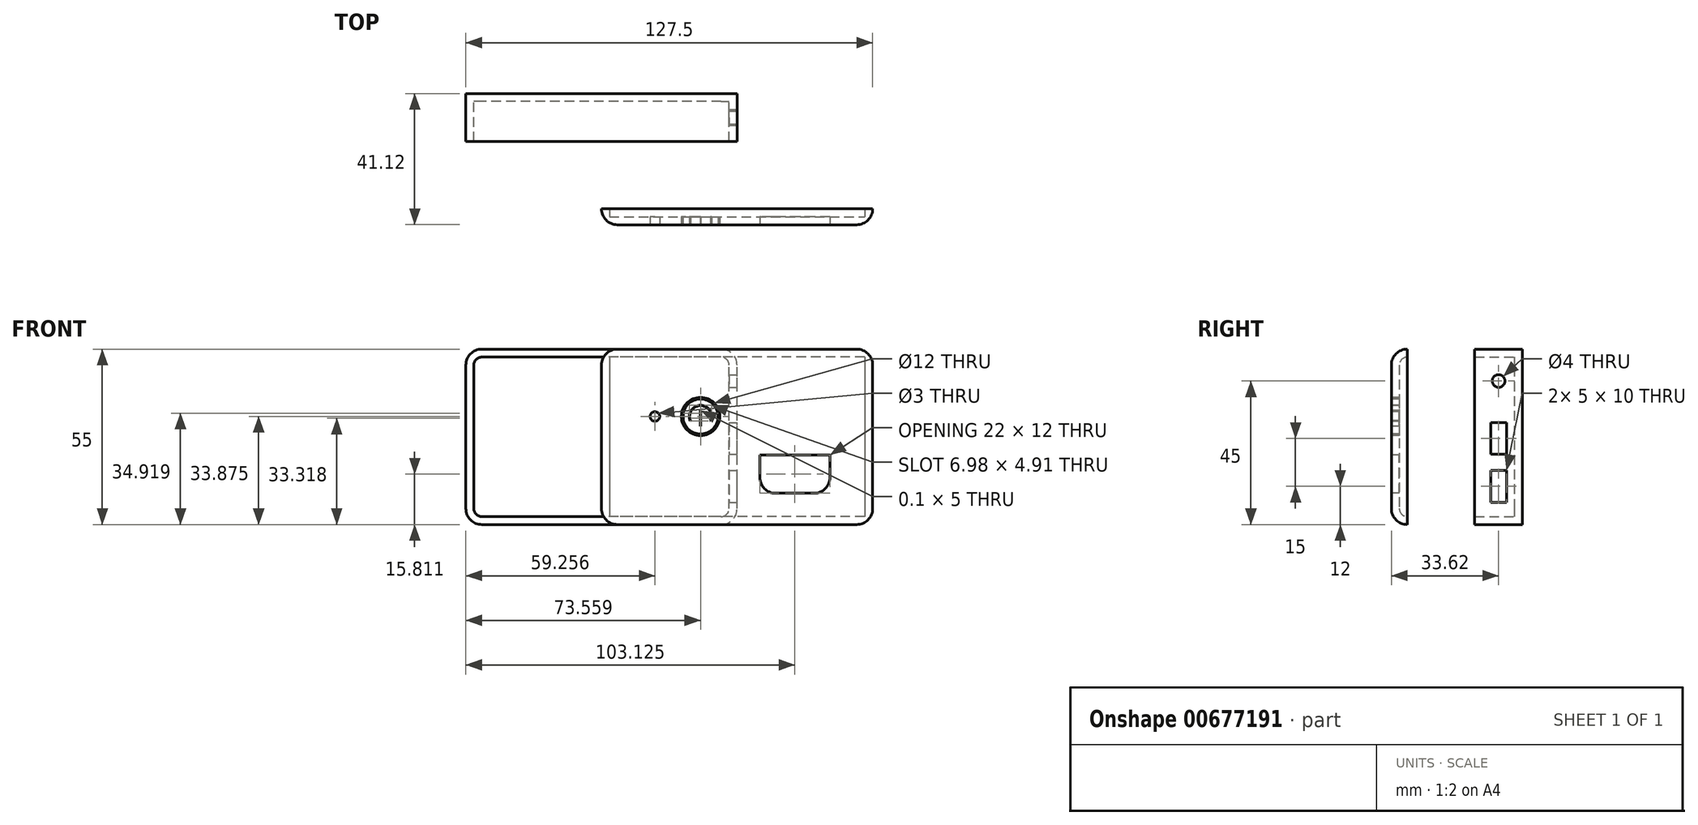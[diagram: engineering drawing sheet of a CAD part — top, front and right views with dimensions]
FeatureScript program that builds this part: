
annotation { "Feature Type Name" : "Feature", "Feature Type Description" : "" }
export const myFeature = defineFeature(function(context is Context, id is Id, definition is map)
    precondition{}
    {
        {
            var Q0;
            Q0=qCreatedBy(makeId("Front.planeOp"),FACE);
            var sketch = newSketch(context, id + "F0", { "sketchPlane" : qUnion([Q0])});
            skLineSegment(sketch, "E0.bottom", {"start": v(42.5, -27.5) * mm, "end": v(-42.5, -27.5) * mm});
            skLineSegment(sketch, "E0.top", {"start": v(42.5, 27.5) * mm, "end": v(-42.5, 27.5) * mm});
            skLineSegment(sketch, "E0.left", {"start": v(42.5, -27.5) * mm, "end": v(42.5, 27.5) * mm});
            skLineSegment(sketch, "E0.right", {"start": v(-42.5, -27.5) * mm, "end": v(-42.5, 27.5) * mm});
            skPoint(sketch, "E0.middle", {"position": v(0, 0) * mm});
            skSolve(sketch);
        }
        {
            var Q0;
            Q0 = qSketchRegion(id + "F0", true);
            extrude(context, id + "F1", {"entities" : qUnion([Q0]), "endBound" : BoundingType.SYMMETRIC, "depth" : 15 * mm, "offsetDistance" : 25 * mm});
        }
        {
            var Q0;
            Q0=makeQuery(id+"F1.opExtrude","SWEPT_EDGE",EDGE,{"disambiguationData":[OSD([sQuery(id+"F0.wireOp",EDGE,"E0.top"),sQuery(id+"F0.wireOp",EDGE,"E0.right")])]});
            var Q1;
            Q1=makeQuery(id+"F1.opExtrude","SWEPT_EDGE",EDGE,{"disambiguationData":[OSD([sQuery(id+"F0.wireOp",EDGE,"E0.top"),sQuery(id+"F0.wireOp",EDGE,"E0.left")])]});
            var Q2;
            Q2=makeQuery(id+"F1.opExtrude","SWEPT_EDGE",EDGE,{"disambiguationData":[OSD([sQuery(id+"F0.wireOp",EDGE,"E0.bottom"),sQuery(id+"F0.wireOp",EDGE,"E0.left")])]});
            var Q3;
            Q3=makeQuery(id+"F1.opExtrude","SWEPT_EDGE",EDGE,{"disambiguationData":[OSD([sQuery(id+"F0.wireOp",EDGE,"E0.bottom"),sQuery(id+"F0.wireOp",EDGE,"E0.right")])]});
            fillet(context, id + "F2", {"entities" : qUnion([Q0, Q1, Q2, Q3]), "radius" : 5 * mm, "tangentPropagation" : true, "allowEdgeOverflow" : false});
        }
        {
            var Q0;
            Q0=makeQuery(id+"F1.opExtrude","CAP_FACE",FACE,{"disambiguationData":[OSD([sQuery(id+"F0.wireOp",EDGE,"E0.bottom"),sQuery(id+"F0.wireOp",EDGE,"E0.top"),sQuery(id+"F0.wireOp",EDGE,"E0.left"),sQuery(id+"F0.wireOp",EDGE,"E0.right")])],"isStart":false});
            shell(context, id + "F3", {"entities" : qUnion([Q0]), "thickness" : 2.5 * mm});
        }
        {
            var Q0;
            Q0=makeQuery(id+"F1.opExtrude","SWEPT_FACE",FACE,{"disambiguationData":[OSD([sQuery(id+"F0.wireOp",EDGE,"E0.left")])]});
            var sketch = newSketch(context, id + "F4", { "sketchPlane" : qUnion([Q0])});
            skLineSegment(sketch, "E1.bottom", {"start": v(2.5, -20.5) * mm, "end": v(-2.5, -20.5) * mm});
            skLineSegment(sketch, "E1.top", {"start": v(2.5, -10.5) * mm, "end": v(-2.5, -10.5) * mm});
            skLineSegment(sketch, "E1.left", {"start": v(2.5, -20.5) * mm, "end": v(2.5, -10.5) * mm});
            skLineSegment(sketch, "E1.right", {"start": v(-2.5, -20.5) * mm, "end": v(-2.5, -10.5) * mm});
            skPoint(sketch, "E1.middle", {"position": v(0, -15.5) * mm});
            skLineSegment(sketch, "E2.bottom", {"start": v(2.5, -5.5) * mm, "end": v(-2.5, -5.5) * mm});
            skLineSegment(sketch, "E2.top", {"start": v(2.5, 4.5) * mm, "end": v(-2.5, 4.5) * mm});
            skLineSegment(sketch, "E2.left", {"start": v(2.5, -5.5) * mm, "end": v(2.5, 4.5) * mm});
            skLineSegment(sketch, "E2.right", {"start": v(-2.5, -5.5) * mm, "end": v(-2.5, 4.5) * mm});
            skPoint(sketch, "E2.middle", {"position": v(0, -0.5) * mm});
            skSolve(sketch);
        }
        {
            var Q0;
            Q0 = qSketchRegion(id + "F4", true);
            extrude(context, id + "F5", {"entities" : qUnion([Q0]), "operationType" : NewBodyOperationType.REMOVE, "oppositeDirection" : true, "depth" : 25 * mm, "offsetDistance" : 25 * mm});
        }
        {
            var Q0;
            Q0=makeQuery(id+"F1.opExtrude","SWEPT_FACE",FACE,{"disambiguationData":[OSD([sQuery(id+"F0.wireOp",EDGE,"E0.left")])]});
            var sketch = newSketch(context, id + "F6", { "sketchPlane" : qUnion([Q0])});
            skCircle(sketch, "E3", {"center": v(0, 17.5) * mm, "radius": 2 * mm});
            skSolve(sketch);
        }
        {
            var Q0;
            Q0 = qSketchRegion(id + "F6", true);
            extrude(context, id + "F7", {"entities" : qUnion([Q0]), "operationType" : NewBodyOperationType.REMOVE, "oppositeDirection" : true, "depth" : 25 * mm, "offsetDistance" : 25 * mm});
        }
        {
            var Q0;
            Q0=qCreatedBy(makeId("Right.planeOp"),FACE);
            var sketch = newSketch(context, id + "F8", { "sketchPlane" : qUnion([Q0])});
            skLineSegment(sketch, "E4", {"start": v(-28.62, 27.5) * mm, "end": v(-28.62, -27.5) * mm});
            skLineSegment(sketch, "E5", {"start": v(-33.62, 22.5) * mm, "end": v(-33.62, -22.5) * mm});
            skArc(sketch, "E6", {"start": v(-28.62, 27.5) * mm, "mid": v(-32.16, 26.04) * mm, "end": v(-33.62, 22.5) * mm});
            skArc(sketch, "E7", {"start": v(-33.62, -22.5) * mm, "mid": v(-32.16, -26.04) * mm, "end": v(-28.62, -27.5) * mm});
            skSolve(sketch);
        }
        {
            var Q0;
            Q0 = qSketchRegion(id + "F8", true);
            extrude(context, id + "F9", {"entities" : qUnion([Q0]), "depth" : 85 * mm, "offsetDistance" : 25 * mm});
        }
        {
            var Q0;
            Q0=makeQuery(id+"F9.opExtrude","SWEPT_FACE",FACE,{"disambiguationData":[OSD([sQuery(id+"F8.wireOp",EDGE,"E4")])]});
            shell(context, id + "F10", {"entities" : qUnion([Q0]), "thickness" : 2.5 * mm});
        }
        {
            var Q0;
            Q0=makeQuery(id+"F9.opExtrude","SWEPT_FACE",FACE,{"disambiguationData":[OSD([sQuery(id+"F8.wireOp",EDGE,"E5")])]});
            var sketch = newSketch(context, id + "F11", { "sketchPlane" : qUnion([Q0])});
            skCircle(sketch, "E8", {"center": v(31.06, 6.37) * mm, "radius": 6 * mm});
            skCircle(sketch, "E9", {"center": v(16.76, 6.37) * mm, "radius": 1.5 * mm});
            skCircle(sketch, "E10", {"center": v(31.06, 6.37) * mm, "radius": 5.5 * mm});
            skArc(sketch, "E11", {"start": v(34.02, 4.1) * mm, "mid": v(31.19, 10.06) * mm, "end": v(27.93, 4.32) * mm});
            skLineSegment(sketch, "E12", {"start": v(31.06, 8.87) * mm, "end": v(31.06, 3.22) * mm});
            skSolve(sketch);
        }
        {
            var Q0;
            Q0 = qSketchRegion(id + "F11", true);
            extrude(context, id + "F12", {"entities" : qUnion([Q0]), "operationType" : NewBodyOperationType.REMOVE, "oppositeDirection" : true, "depth" : 25 * mm, "offsetDistance" : 25 * mm});
        }
        {
            var Q0;
            Q0=makeQuery(id+"F9.opExtrude","SWEPT_FACE",FACE,{"disambiguationData":[OSD([sQuery(id+"F8.wireOp",EDGE,"E5")])]});
            var sketch = newSketch(context, id + "F13", { "sketchPlane" : qUnion([Q0])});
            skLineSegment(sketch, "E13.bottom", {"start": v(49.63, -5.69) * mm, "end": v(71.63, -5.69) * mm});
            skLineSegment(sketch, "E13.top", {"start": v(54.63, -17.69) * mm, "end": v(66.63, -17.69) * mm});
            skLineSegment(sketch, "E13.left", {"start": v(49.63, -5.69) * mm, "end": v(49.63, -12.69) * mm});
            skLineSegment(sketch, "E13.right", {"start": v(71.63, -5.69) * mm, "end": v(71.63, -12.69) * mm});
            skPoint(sketch, "E14.visualSharp", {"position": v(49.63, -17.69) * mm});
            skArc(sketch, "E14.filletArc", {"start": v(49.63, -12.69) * mm, "mid": v(51.09, -16.22) * mm, "end": v(54.63, -17.69) * mm});
            skPoint(sketch, "E15.visualSharp", {"position": v(71.63, -17.69) * mm});
            skArc(sketch, "E15.filletArc", {"start": v(66.63, -17.69) * mm, "mid": v(70.16, -16.22) * mm, "end": v(71.63, -12.69) * mm});
            skSolve(sketch);
        }
        {
            var Q0;
            Q0 = qSketchRegion(id + "F13", true);
            extrude(context, id + "F14", {"entities" : qUnion([Q0]), "operationType" : NewBodyOperationType.REMOVE, "oppositeDirection" : true, "depth" : 25 * mm, "offsetDistance" : 25 * mm});
        }
        {
            var Q0;
            Q0=makeQuery(id+"F12.boolean.opBoolean","SPLIT",FACE,{"disambiguationData":[TD([makeQuery(id+"F12.opExtrude","SWEPT_FACE",FACE,{"disambiguationData":[OSD([sQuery(id+"F11.wireOp",EDGE,"E10")])]})])],"derivedFrom":makeQuery(id+"F9.opExtrude","SWEPT_FACE",FACE,{"disambiguationData":[OSD([sQuery(id+"F8.wireOp",EDGE,"E5")])]})});
            var sketch = newSketch(context, id + "F15", { "sketchPlane" : qUnion([Q0])});
            skArc(sketch, "E16", {"start": v(34.26, 4.96) * mm, "mid": v(31.06, 9.87) * mm, "end": v(27.86, 4.96) * mm});
            skArc(sketch, "E17", {"start": v(34.2, 5.07) * mm, "mid": v(31.06, 9.77) * mm, "end": v(27.92, 5.07) * mm});
            skPoint(sketch, "E18", {"position": v(27.92, 5.07) * mm});
            skPoint(sketch, "E19", {"position": v(34.2, 5.07) * mm});
            skPoint(sketch, "E20", {"position": v(27.86, 4.96) * mm});
            skPoint(sketch, "E21", {"position": v(34.26, 4.96) * mm});
            skLineSegment(sketch, "E22", {"start": v(27.86, 4.96) * mm, "end": v(27.92, 5.07) * mm});
            skLineSegment(sketch, "E23", {"start": v(34.2, 5.07) * mm, "end": v(34.26, 4.96) * mm});
            skLineSegment(sketch, "E24", {"start": v(31, 8.32) * mm, "end": v(31, 3.32) * mm});
            skLineSegment(sketch, "E25", {"start": v(31, 8.32) * mm, "end": v(31.1, 8.32) * mm});
            skLineSegment(sketch, "E26", {"start": v(31.1, 8.32) * mm, "end": v(31.1, 3.32) * mm});
            skLineSegment(sketch, "E27", {"start": v(31.1, 3.32) * mm, "end": v(31, 3.32) * mm});
            skSolve(sketch);
        }
        {
            var Q0;
            Q0 = qSketchRegion(id + "F15", true);
            extrude(context, id + "F16", {"entities" : qUnion([Q0]), "operationType" : NewBodyOperationType.REMOVE, "oppositeDirection" : true, "depth" : 25 * mm, "offsetDistance" : 25 * mm});
        }
        {
            var Q0;
            Q0=makeQuery(id+"F9.opExtrude","CAP_EDGE",EDGE,{"disambiguationData":[OSD([sQuery(id+"F8.wireOp",EDGE,"E6")])],"isStart":true});
            var Q1;
            Q1=makeQuery(id+"F9.opExtrude","CAP_EDGE",EDGE,{"disambiguationData":[OSD([sQuery(id+"F8.wireOp",EDGE,"E5")])],"isStart":false});
            fillet(context, id + "F17", {"entities" : qUnion([Q0, Q1]), "radius" : 5 * mm, "tangentPropagation" : true, "allowEdgeOverflow" : false});
        }
    });
